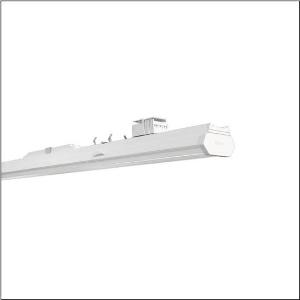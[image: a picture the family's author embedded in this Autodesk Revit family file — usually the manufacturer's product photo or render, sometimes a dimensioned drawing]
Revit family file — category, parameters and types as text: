
# Revit family: licross_r__11_protected_mo_51td11cn49xg_045e
name_source: partatom
category: Lighting Fixtures
units: mm (PartAtom-declared; Revit-internal decimal feet)

## family parameters
Cut with Voids When Loaded = No
Host = Face
Light Source = No
Part Type = Normal
Room Calculation Point = No
Round Connector Dimension = Use Diameter
Shared = No

## types (1)
- --- (1 x LED, 9030 lm, 49.4 W, 4000K)
    Apparent Load = 49 VA
    CIE Flux Codes = 83 94 98 100 100
    Color Rendering = 80
    Color Temperature = 4000K
    Default Elevation = 1800 mm
    Description = Licross® 11 Protected MO, luminaire insert, of sheet steel, galvanised, coil coated, white, length: 1.500mm, width: 90mm, height: 101mm, LED rated luminous flux: 9.030lm, light colour: 840, control gear: ON/OFF Multilumen, CLOi, with plug, 3-pole, with phase selection, mains connection: 220..240V, AC, 50/60Hz, start of lifetime: 49W, end of service life: 55W, halogen-free wiring, primary light control with lens, of plastic, primary optical cover: cover, of PMMA, light emission: direct distribution, primary light characteristic: symmetric, protection rating (complete): IP54, insulation class (complete): insulation class I (protective earthing), certification: CE, ENEC, VDE, UKCA, protection symbol: D if used in an environment with non-conductive dust loads with corresponding accessories, impact resistance: IK06, permissible ambient temperature for indoor applications: -35..+40°C, corresponds to IFS (International Featured Standards) requirements for safety and quality in the food industry, reducing of maximum allowable ambient temperature of 5°C with ceiling mounting, LABS conformity tested according to VDMA 24364:2018-05, packaging unit: 1 piece
    Height = 92 mm
    Lamp = 1 x LED
    Lamp Light Flux = 9030 lm
    Lamp Power = 49.4 W
    Lamp count = 1
    Length = 1500 mm
    Luminous efficacy = 183 lm/W
    Manufacturer = Siteco
    ModVariant = No
    Model = 51TD11CN49XG
    Mounting Place = Ceiling
    Mounting Type = Pendant
    Number of Poles = 1
    OnlyDefault = Yes
    Power Factor = 1
    Product Name = Licross® 11 Protected MO
    Product group = luminaire insert
    ProductGroupID = 901
    Protection Class = Protection class I
    Protection Degree = IP 54
    RLX_Detail_Level = 1
    RLX_Emergency_Light_Flux = 0 lm
    RLX_Emergency_Type = 0
    RLX_Emergency_Type_DB = No
    RlxData = <blob elided: 21849 chars, md5=e366b63d>
    Socket = socket
    Standby Power = 0 W
    System Light Flux = 9030 lm
    System Power = 49 W
    Type Comments = factory setting: luminous flux: 100 % | (A | C | E) | 113 mA
    Type Image = l_1256145.jpg
    URL = http://relux.com
    VarID = @adj_055119
    Voltage = 0 V
    Weight = 0.00 kg
    Width = 88 mm

## geometry (parser evidence)
native form markers: Blend x4, Sweep x10
no freeform markers — native parametric forms only
